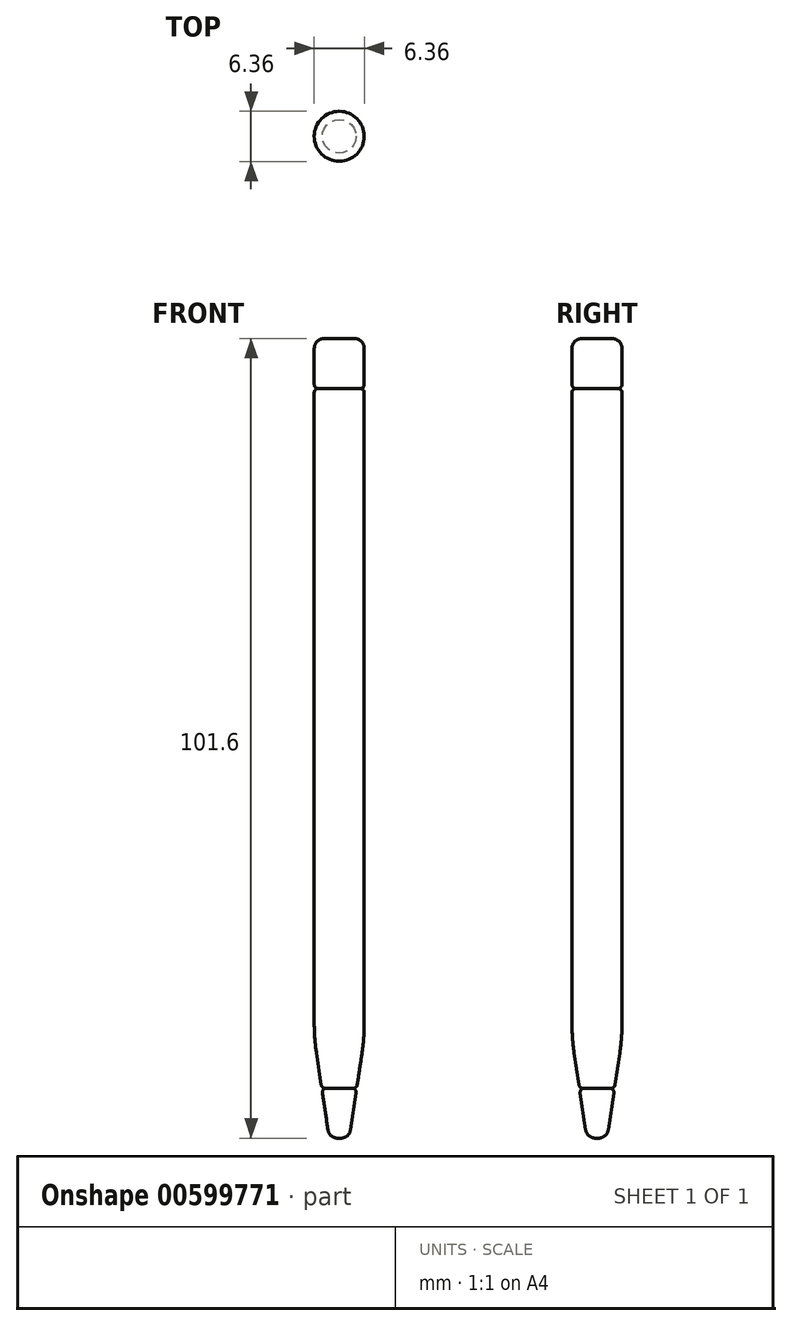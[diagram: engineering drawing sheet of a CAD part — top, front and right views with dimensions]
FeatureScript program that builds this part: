
annotation { "Feature Type Name" : "Feature", "Feature Type Description" : "" }
export const myFeature = defineFeature(function(context is Context, id is Id, definition is map)
    precondition{}
    {
        {
            var Q0;
            Q0=qCreatedBy(makeId("Front.planeOp"),FACE);
            var sketch = newSketch(context, id + "F0", { "sketchPlane" : qUnion([Q0])});
            skLineSegment(sketch, "E0", {"start": v(0, 101.6) * mm, "end": v(3.18, 101.6) * mm});
            skLineSegment(sketch, "E1", {"start": v(3.18, 101.6) * mm, "end": v(3.18, 12.7) * mm});
            skLineSegment(sketch, "E2", {"start": v(0, 101.6) * mm, "end": v(0, 0) * mm});
            skLineSegment(sketch, "E3", {"start": v(3.18, 12.7) * mm, "end": v(1.27, 0) * mm});
            skLineSegment(sketch, "E4", {"start": v(1.27, 0) * mm, "end": v(0, 0) * mm});
            skLineSegment(sketch, "E5", {"start": v(3.18, 95.25) * mm, "end": v(0, 95.25) * mm});
            skLineSegment(sketch, "E6", {"start": v(0, 6.35) * mm, "end": v(2.22, 6.35) * mm});
            skSolve(sketch);
        }
        {
            var Q0;
            {var subQ4=sQuery(id+"F0.wireOp",EDGE,"E5");Q0=makeQuery(id+"F0.imprint","IMPRINT",FACE,{"disambiguationData":[TD([[makeQuery(id+"F0.imprint","IMPRINT",EDGE,{"derivedFrom":subQ4}),1.0]])]});}
            var Q1;
            Q1=sQuery(id+"F0.wireOp",EDGE,"E2");
            revolve(context, id + "F1", {"entities" : qUnion([Q0]), "axis" : qUnion([Q1]), "revolveType" : RevolveType.FULL});
        }
        {
            var Q0;
            {var subQ0=sQuery(id+"F0.wireOp",EDGE,"E0");Q0=makeQuery(id+"F0.imprint","IMPRINT",FACE,{"disambiguationData":[TD([[makeQuery(id+"F0.imprint","IMPRINT",EDGE,{"derivedFrom":subQ0}),-1.0]])]});}
            var Q1;
            {var subQ0=sQuery(id+"F0.wireOp",EDGE,"E4");Q1=makeQuery(id+"F0.imprint","IMPRINT",FACE,{"disambiguationData":[TD([[makeQuery(id+"F0.imprint","IMPRINT",EDGE,{"derivedFrom":subQ0}),-1.0]])]});}
            var Q2;
            Q2=sQuery(id+"F0.wireOp",EDGE,"E2");
            revolve(context, id + "F2", {"entities" : qUnion([Q0, Q1]), "axis" : qUnion([Q2]), "revolveType" : RevolveType.FULL});
        }
        {
            var Q0;
            Q0=makeQuery(id+"F1.opRevolve","SWEPT_EDGE",EDGE,{"disambiguationData":[OSD([sQuery(id+"F0.wireOp",EDGE,"E3"),sQuery(id+"F0.wireOp",EDGE,"E6")])]});
            var Q1;
            Q1=makeQuery(id+"F1.opRevolve","SWEPT_EDGE",EDGE,{"disambiguationData":[OSD([sQuery(id+"F0.wireOp",EDGE,"E1"),sQuery(id+"F0.wireOp",EDGE,"E5")])]});
            var Q2;
            Q2=makeQuery(id+"F2.opRevolve","SWEPT_EDGE",EDGE,{"disambiguationData":[OSD([sQuery(id+"F0.wireOp",EDGE,"E3"),sQuery(id+"F0.wireOp",EDGE,"E6")])]});
            var Q3;
            Q3=makeQuery(id+"F2.opRevolve","SWEPT_EDGE",EDGE,{"disambiguationData":[OSD([sQuery(id+"F0.wireOp",EDGE,"E1"),sQuery(id+"F0.wireOp",EDGE,"E5")])]});
            fillet(context, id + "F3", {"entities" : qUnion([Q0, Q1, Q2, Q3]), "radius" : 0.5 * mm, "tangentPropagation" : true, "allowEdgeOverflow" : false});
        }
        {
            var Q0;
            Q0=makeQuery(id+"F2.opRevolve","SWEPT_EDGE",EDGE,{"disambiguationData":[OSD([sQuery(id+"F0.wireOp",EDGE,"E3"),sQuery(id+"F0.wireOp",EDGE,"E4")])]});
            var Q1;
            Q1=makeQuery(id+"F2.opRevolve","SWEPT_EDGE",EDGE,{"disambiguationData":[OSD([sQuery(id+"F0.wireOp",EDGE,"E0"),sQuery(id+"F0.wireOp",EDGE,"E1")])]});
            fillet(context, id + "F4", {"entities" : qUnion([Q0, Q1]), "radius" : 1.27 * mm, "tangentPropagation" : true, "allowEdgeOverflow" : false});
        }
        {
            var Q0;
            Q0=makeQuery(id+"F1.opRevolve","SWEPT_EDGE",EDGE,{"disambiguationData":[OSD([sQuery(id+"F0.wireOp",EDGE,"E1"),sQuery(id+"F0.wireOp",EDGE,"E3")])]});
            fillet(context, id + "F5", {"entities" : qUnion([Q0]), "radius" : 25.4 * mm, "tangentPropagation" : true, "allowEdgeOverflow" : false});
        }
    });
